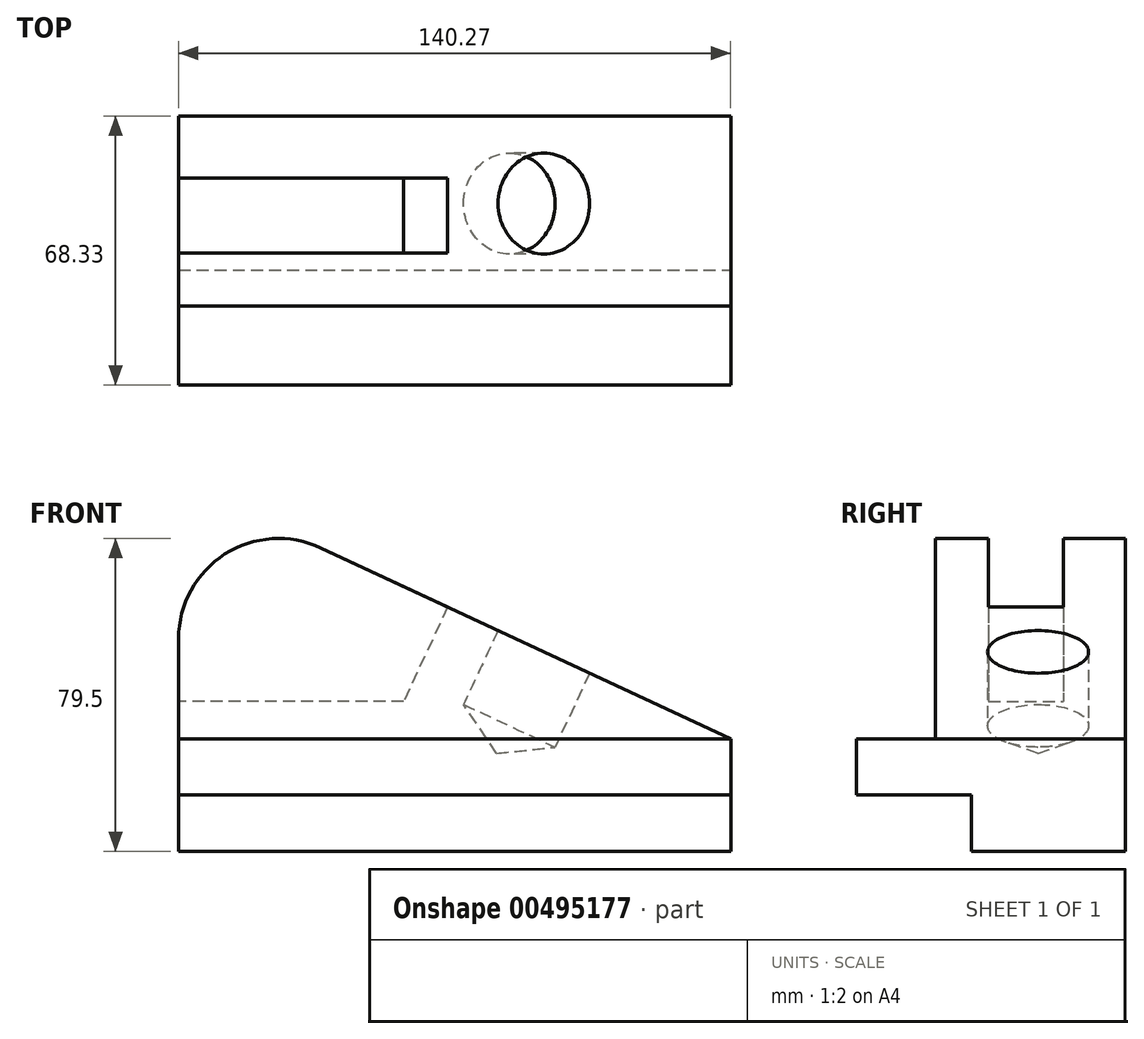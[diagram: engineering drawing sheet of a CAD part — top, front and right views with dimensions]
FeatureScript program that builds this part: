
annotation { "Feature Type Name" : "Feature", "Feature Type Description" : "" }
export const myFeature = defineFeature(function(context is Context, id is Id, definition is map)
    precondition{}
    {
        {
            var Q0;
            Q0=qCreatedBy(makeId("Front.planeOp"),FACE);
            var sketch = newSketch(context, id + "F0", { "sketchPlane" : qUnion([Q0])});
            skPoint(sketch, "E0.visualSharp", {"position": v(-130.52, 100.67) * mm});
            skLineSegment(sketch, "E1", {"start": v(-86.73, 0) * mm, "end": v(-86.73, -14.34) * mm});
            skLineSegment(sketch, "E2", {"start": v(-86.73, -14.34) * mm, "end": v(53.54, -14.34) * mm});
            skLineSegment(sketch, "E3", {"start": v(53.54, -14.34) * mm, "end": v(53.54, 0) * mm});
            skLineSegment(sketch, "E4", {"start": v(-86.73, 0) * mm, "end": v(53.54, 0) * mm});
            skLineSegment(sketch, "E5", {"start": v(53.54, 14.22) * mm, "end": v(-86.73, 14.22) * mm});
            skLineSegment(sketch, "E6", {"start": v(-86.73, 14.22) * mm, "end": v(-86.73, 0) * mm});
            skLineSegment(sketch, "E7", {"start": v(53.54, 14.22) * mm, "end": v(53.54, 0) * mm});
            skLineSegment(sketch, "E8", {"start": v(-86.73, 14.22) * mm, "end": v(-86.73, 39.76) * mm});
            skLineSegment(sketch, "E9", {"start": v(-50.6, 62.78) * mm, "end": v(53.54, 14.22) * mm});
            skPoint(sketch, "E10.visualSharp", {"position": v(-86.73, 79.63) * mm});
            skArc(sketch, "E10.filletArc", {"start": v(-50.6, 62.78) * mm, "mid": v(-74.98, 61.19) * mm, "end": v(-86.73, 39.76) * mm});
            skSolve(sketch);
        }
        {
            var Q0;
            Q0 = qSketchRegion(id + "F0", true);
            extrude(context, id + "F1", {"entities" : qUnion([Q0]), "depth" : 68.33 * mm});
        }
        {
            var Q0;
            Q0=makeQuery(id+"F1.opExtrude","SWEPT_FACE",FACE,{"disambiguationData":[OSD([sQuery(id+"F0.wireOp",EDGE,"E3"),sQuery(id+"F0.wireOp",EDGE,"E7")])]});
            var sketch = newSketch(context, id + "F2", { "sketchPlane" : qUnion([Q0])});
            skLineSegment(sketch, "E11.bottom", {"start": v(-68.33, -14.34) * mm, "end": v(-39.12, -14.34) * mm});
            skLineSegment(sketch, "E11.top", {"start": v(-68.33, 0) * mm, "end": v(-39.12, 0) * mm});
            skLineSegment(sketch, "E11.left", {"start": v(-68.33, -14.34) * mm, "end": v(-68.33, 0) * mm});
            skLineSegment(sketch, "E11.right", {"start": v(-39.12, -14.34) * mm, "end": v(-39.12, 0) * mm});
            skSolve(sketch);
        }
        {
            var Q0;
            Q0 = qSketchRegion(id + "F2", true);
            extrude(context, id + "F3", {"entities" : qUnion([Q0]), "operationType" : NewBodyOperationType.REMOVE, "endBound" : BoundingType.THROUGH_ALL, "oppositeDirection" : true, "depth" : 25.4 * mm});
        }
        {
            var Q0;
            Q0=makeQuery(id+"F1.opExtrude","SWEPT_FACE",FACE,{"disambiguationData":[OSD([sQuery(id+"F0.wireOp",EDGE,"E3"),sQuery(id+"F0.wireOp",EDGE,"E7")])]});
            var sketch = newSketch(context, id + "F4", { "sketchPlane" : qUnion([Q0])});
            skLineSegment(sketch, "E12.bottom", {"start": v(-48.26, 14.22) * mm, "end": v(-95.63, 14.22) * mm});
            skLineSegment(sketch, "E12.top", {"start": v(-48.26, 74.65) * mm, "end": v(-95.63, 74.65) * mm});
            skLineSegment(sketch, "E12.left", {"start": v(-48.26, 14.22) * mm, "end": v(-48.26, 74.65) * mm});
            skLineSegment(sketch, "E12.right", {"start": v(-95.63, 14.22) * mm, "end": v(-95.63, 74.65) * mm});
            skSolve(sketch);
        }
        {
            var Q0;
            Q0 = qSketchRegion(id + "F4", true);
            extrude(context, id + "F5", {"entities" : qUnion([Q0]), "operationType" : NewBodyOperationType.REMOVE, "endBound" : BoundingType.THROUGH_ALL, "oppositeDirection" : true, "depth" : 25.4 * mm});
        }
        {
            var Q0;
            Q0=qCreatedBy(makeId("Front.planeOp"),FACE);
            cPlane(context, id + "F6", {"entities" : qUnion([Q0]), "cplaneType" : CPlaneType.OFFSET, "offset" : 15.75 * mm, "width" : 152.4 * mm, "height" : 152.4 * mm});
        }
        {
            var Q0;
            Q0=qCreatedBy(id+"F6.planeOp",FACE);
            var sketch = newSketch(context, id + "F7", { "sketchPlane" : qUnion([Q0])});
            skLineSegment(sketch, "E13", {"start": v(-8.69, 68.53) * mm, "end": v(-29.59, 23.71) * mm});
            skLineSegment(sketch, "E14", {"start": v(-29.59, 23.71) * mm, "end": v(-100.32, 23.71) * mm});
            skLineSegment(sketch, "E15", {"start": v(-100.32, 23.71) * mm, "end": v(-100.32, 74.68) * mm});
            skLineSegment(sketch, "E16", {"start": v(-100.32, 74.68) * mm, "end": v(-8.69, 68.53) * mm});
            skSolve(sketch);
        }
        {
            var Q0;
            Q0=makeQuery(id+"F7.imprint","IMPRINT",FACE,{"disambiguationData":[TD([[makeQuery(id+"F7.imprint","IMPRINT",EDGE,{"derivedFrom":sQuery(id+"F7.wireOp",EDGE,"E13")}),-1.0]])]});
            extrude(context, id + "F8", {"entities" : qUnion([Q0]), "operationType" : NewBodyOperationType.REMOVE, "depth" : 19.05 * mm, "offsetDistance" : 25.4 * mm});
        }
        {
            var Q0;
            Q0=qCreatedBy(makeId("Front.planeOp"),FACE);
            cPlane(context, id + "F9", {"entities" : qUnion([Q0]), "cplaneType" : CPlaneType.OFFSET, "offset" : 22.22 * mm, "width" : 152.4 * mm, "height" : 152.4 * mm});
        }
        {
            var Q0;
            Q0=qCreatedBy(id+"F9.planeOp",FACE);
            var sketch = newSketch(context, id + "F10", { "sketchPlane" : qUnion([Q0])});
            skLineSegment(sketch, "E17", {"start": v(11.63, 48.26) * mm, "end": v(-5.95, 10.58) * mm});
            skLineSegment(sketch, "E18", {"start": v(-5.95, 10.58) * mm, "end": v(-14.32, 22.98) * mm});
            skLineSegment(sketch, "E19", {"start": v(-14.32, 22.98) * mm, "end": v(0, 53.68) * mm});
            skLineSegment(sketch, "E20", {"start": v(0, 53.68) * mm, "end": v(11.63, 48.26) * mm});
            skSolve(sketch);
        }
        {
            var Q0;
            Q0=makeQuery(id+"F10.imprint","IMPRINT",FACE,{"disambiguationData":[TD([[makeQuery(id+"F10.imprint","IMPRINT",EDGE,{"derivedFrom":sQuery(id+"F10.wireOp",EDGE,"E17")}),-1.0]])]});
            var Q1;
            Q1=sQuery(id+"F10.wireOp",EDGE,"E20");
            var Q2;
            Q2=sQuery(id+"F10.wireOp",EDGE,"E18");
            var Q3;
            Q3=sQuery(id+"F10.wireOp",EDGE,"E19");
            var Q4;
            Q4=sQuery(id+"F10.wireOp",EDGE,"E17");
            revolve(context, id + "F11", {"operationType" : NewBodyOperationType.REMOVE, "entities" : qUnion([Q0]), "surfaceEntities" : qUnion([Q1, Q2, Q3]), "axis" : qUnion([Q4]), "revolveType" : RevolveType.FULL, "oppositeDirection" : true});
        }
    });
